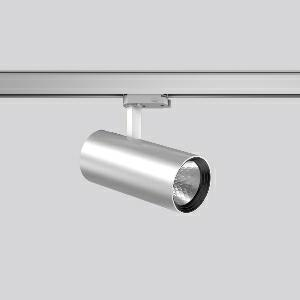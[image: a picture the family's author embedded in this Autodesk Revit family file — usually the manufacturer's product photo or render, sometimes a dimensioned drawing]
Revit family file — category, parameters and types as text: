
# Revit family: deecos_s_mini_742195_004_89ca
name_source: partatom
category: Lighting Fixtures
units: mm (PartAtom-declared; Revit-internal decimal feet)

## family parameters
Cut with Voids When Loaded = No
Host = Face
Light Source = No
Part Type = Normal
Room Calculation Point = No
Round Connector Dimension = Use Diameter
Shared = No

## types (1)
- DEECOS S mini (1 x LED Modul 930, 2500 lm, 3000)
    Apparent Load = 20 VA
    Approval mark = CE
    CIE Flux Codes = 100 100 100 100 100
    Color Rendering = 90
    Color Temperature = 3000
    Default Elevation = 1800 mm
    Description = Series: DEECOS S mini
LED surface-mounted projector in modern design with no visible cooling ribs. Housing: die-cast aluminium, powder-coated. Rotation range: 356°. Swivel range: 90°. Black plastic ring and recessed LED to prevent glare from the side. Optical assembly with reflector made of MIRO-Silver with 98% total light reflection for outstanding efficiency - can be changed without tools. Best colour rendering index Ra>90. With multi adaptor for 3-circuit tracks 230 V. Suitable for Track on ceiling, Wall track. High quality converter without flickering and stroboscopic effect. The following accessories can be mounted without use of tools: interchangeable lenses, decorative glasses, honeycomb louvre, clear and frosted diffusers, white interchangeable plastic ring. 
Colour: silver
Diameter: 87 mm
Height: 214 mm
Lamp: LED
Socket: without socket
Colour temperature: 3000K
Colour rendering index (CRI): 92
System power: 20 W
Rated luminous flux: 2500 lm
Luminous efficiency: 125 lm/W
Control gear: Regulated power supply
Protection class: I
Type of protection: IP 20
    Height = 214 mm
    Lamp = 1 x LED Modul 930
    Lamp Light Flux = 2500 lm
    Lamp count = 1
    Length = 87 mm
    Lifetime = 50000 h
    Luminous efficacy = 125 lm/W
    Manufacturer = RZB
    ModVariant = No
    Model = 742195.004
    Mounting Place = Ceiling
    Mounting Type = Rail mounted
    Number of Poles = 1
    OnlyDefault = Yes
    Power Factor = 1
    Product Name = DEECOS S mini
    Product group = Track mounted projectors
    ProductGroupID = 301
    Protection Class = Protection class I
    Protection Degree = IP 20
    RLX_Detail_Level = 1
    RLX_Emergency_Light_Flux = 0 lm
    RLX_Emergency_Type = 0
    RLX_Emergency_Type_DB = No
    RlxData = <blob elided: 37117 chars, md5=337ab036>
    Socket = socket
    Standby Power = 0 W
    System Light Flux = 2500 lm
    System Power = 20 W
    Type Comments = Product without accessories
    Type Image = 741926.004.jpg
    URL = http://relux.com
    VarID = ---
    Voltage = 230 V
    Voltage Range = 220-240 V
    Weight = 0.00 kg
    Width = 0 mm  [stored 0 ft]

note: [stored X ft] marks values corroborated as IEEE doubles in the binary element streams (Revit-internal decimal feet)

## geometry (parser evidence)
native form markers: Blend x4, Sweep x12
no freeform markers — native parametric forms only
